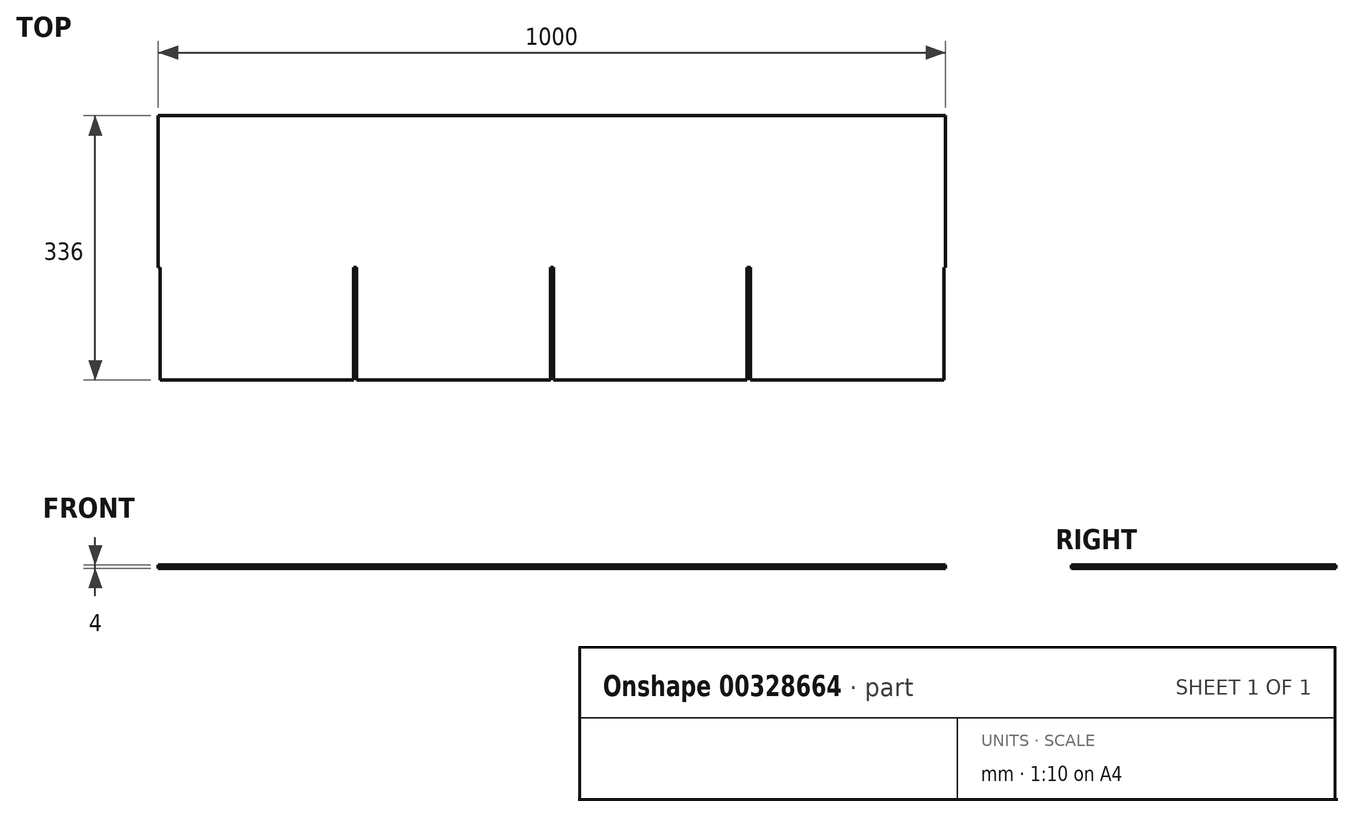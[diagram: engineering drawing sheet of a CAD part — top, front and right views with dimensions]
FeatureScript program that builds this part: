
annotation { "Feature Type Name" : "Feature", "Feature Type Description" : "" }
export const myFeature = defineFeature(function(context is Context, id is Id, definition is map)
    precondition{}
    {
        {
            var Q0;
            Q0=qCreatedBy(makeId("Top.planeOp"),FACE);
            var sketch = newSketch(context, id + "F0", { "sketchPlane" : qUnion([Q0])});
            skLineSegment(sketch, "E0.bottom", {"start": v(0, 0) * mm, "end": v(1000, 0) * mm});
            skLineSegment(sketch, "E0.top", {"start": v(0, -336) * mm, "end": v(248, -336) * mm});
            skLineSegment(sketch, "E0.left", {"start": v(0, 0) * mm, "end": v(0, -193) * mm});
            skLineSegment(sketch, "E0.right", {"start": v(1000, 0) * mm, "end": v(1000, -193) * mm});
            skLineSegment(sketch, "E1", {"start": v(498, -193) * mm, "end": v(498, -336) * mm});
            skLineSegment(sketch, "E2", {"start": v(502, -193) * mm, "end": v(502, -336) * mm});
            skLineSegment(sketch, "E3.trimOffspring", {"start": v(502, -336) * mm, "end": v(748, -336) * mm});
            skLineSegment(sketch, "E4", {"start": v(0, -193) * mm, "end": v(1000, -193) * mm, "construction": true});
            skLineSegment(sketch, "E5", {"start": v(250, 0) * mm, "end": v(250, -193) * mm, "construction": true});
            skLineSegment(sketch, "E6", {"start": v(750, 0) * mm, "end": v(750, -193) * mm, "construction": true});
            skLineSegment(sketch, "E7", {"start": v(500, 0) * mm, "end": v(500, -193) * mm, "construction": true});
            skLineSegment(sketch, "E8", {"start": v(250, -193) * mm, "end": v(248, -193) * mm});
            skLineSegment(sketch, "E9", {"start": v(248, -193) * mm, "end": v(248, -336) * mm});
            skLineSegment(sketch, "E10", {"start": v(250, -193) * mm, "end": v(252, -193) * mm});
            skLineSegment(sketch, "E11", {"start": v(252, -193) * mm, "end": v(252, -336) * mm});
            skLineSegment(sketch, "E12.trimOffspring", {"start": v(252, -336) * mm, "end": v(498, -336) * mm});
            skLineSegment(sketch, "E13", {"start": v(750, -193) * mm, "end": v(748, -193) * mm});
            skLineSegment(sketch, "E14", {"start": v(750, -193) * mm, "end": v(752, -193) * mm});
            skLineSegment(sketch, "E15", {"start": v(748, -193) * mm, "end": v(748, -336) * mm});
            skLineSegment(sketch, "E16", {"start": v(752, -193) * mm, "end": v(752, -336) * mm});
            skLineSegment(sketch, "E17", {"start": v(0, -193) * mm, "end": v(2, -193) * mm});
            skLineSegment(sketch, "E18", {"start": v(2, -193) * mm, "end": v(2, -336) * mm});
            skLineSegment(sketch, "E19", {"start": v(1000, -193) * mm, "end": v(998, -193) * mm});
            skLineSegment(sketch, "E20", {"start": v(998, -193) * mm, "end": v(998, -336) * mm});
            skLineSegment(sketch, "E21", {"start": v(498, -193) * mm, "end": v(500, -193) * mm});
            skLineSegment(sketch, "E22", {"start": v(502, -193) * mm, "end": v(500, -193) * mm});
            skLineSegment(sketch, "E23.trimOffspring", {"start": v(752, -336) * mm, "end": v(998, -336) * mm});
            skSolve(sketch);
        }
        {
            var Q0;
            Q0=qSketchRegion(id+"F0",true);
            extrude(context, id + "F1", {"entities" : qUnion([Q0]), "oppositeDirection" : true, "depth" : 4 * mm});
        }
    });
